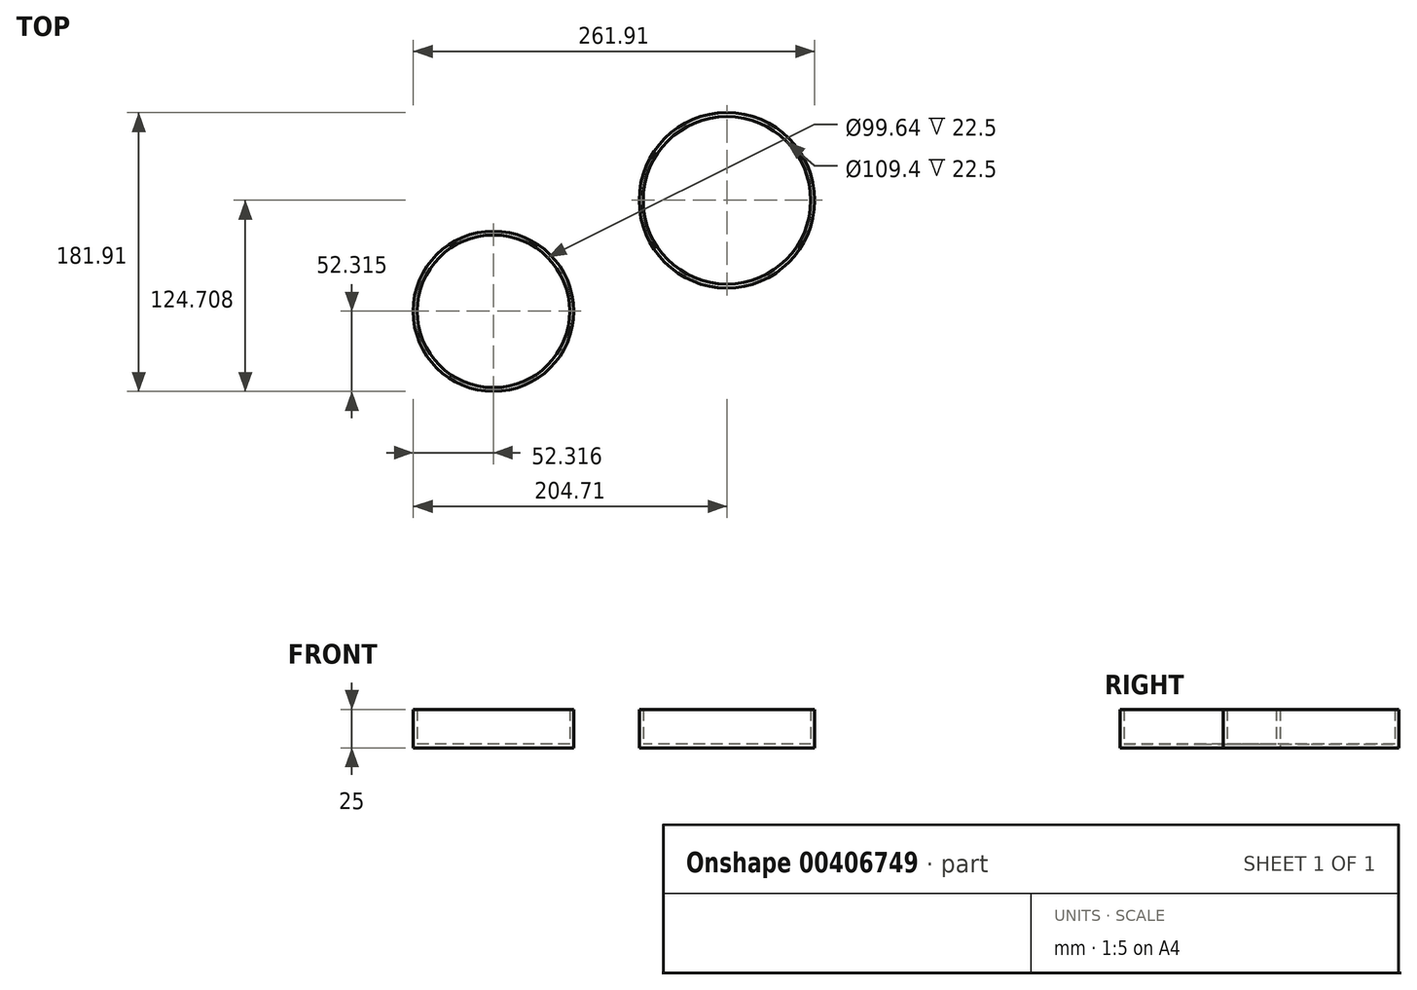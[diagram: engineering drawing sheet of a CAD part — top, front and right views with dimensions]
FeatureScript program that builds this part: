
annotation { "Feature Type Name" : "Feature", "Feature Type Description" : "" }
export const myFeature = defineFeature(function(context is Context, id is Id, definition is map)
    precondition{}
    {
        {
            var Q0;
            Q0=qCreatedBy(makeId("Top.planeOp"),FACE);
            var sketch = newSketch(context, id + "F0", { "sketchPlane" : qUnion([Q0])});
            skCircle(sketch, "E0", {"center": v(-87.18, -47.85) * mm, "radius": 52.32 * mm});
            skCircle(sketch, "E1", {"center": v(65.2, 24.54) * mm, "radius": 57.2 * mm});
            skSolve(sketch);
        }
        {
            var Q0;
            Q0 = qSketchRegion(id + "F0", true);
            extrude(context, id + "F1", {"entities" : qUnion([Q0]), "depth" : 25 * mm});
        }
        {
            var Q0;
            Q0=makeQuery(id+"F1.opExtrude","CAP_FACE",FACE,{"disambiguationData":[OSD([sQuery(id+"F0.wireOp",EDGE,"E0")])],"isStart":false});
            var Q1;
            Q1=makeQuery(id+"F1.opExtrude","CAP_FACE",FACE,{"disambiguationData":[OSD([sQuery(id+"F0.wireOp",EDGE,"E1")])],"isStart":false});
            shell(context, id + "F2", {"entities" : qUnion([Q0, Q1]), "thickness" : 2.5 * mm});
        }
    });
